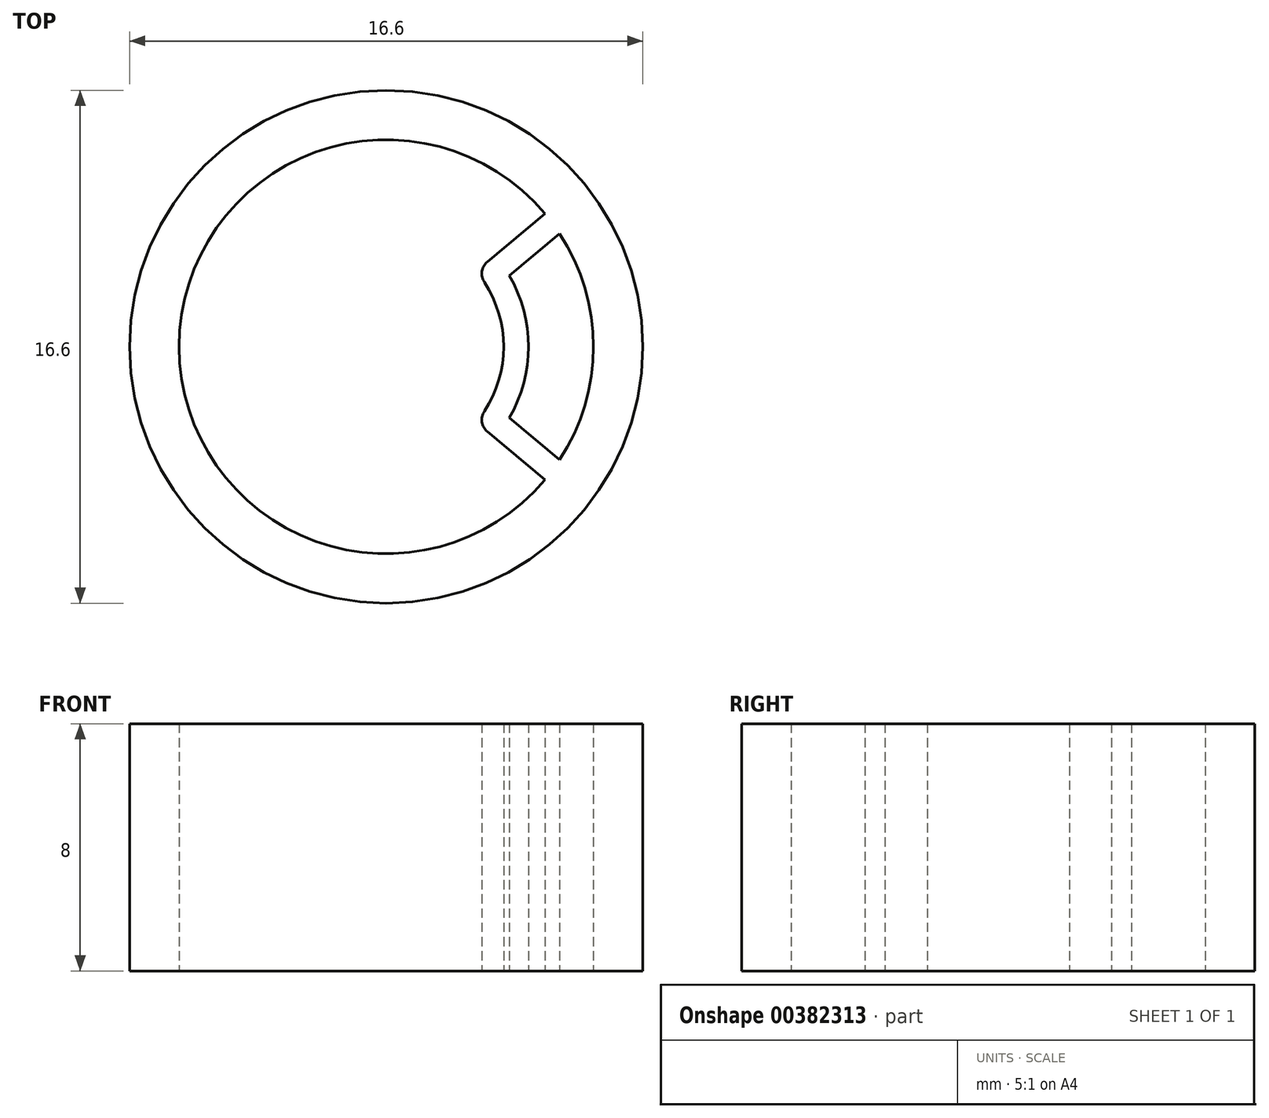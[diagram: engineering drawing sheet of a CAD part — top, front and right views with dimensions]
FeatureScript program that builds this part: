
annotation { "Feature Type Name" : "Feature", "Feature Type Description" : "" }
export const myFeature = defineFeature(function(context is Context, id is Id, definition is map)
    precondition{}
    {
        {
            var Q0;
            Q0=qCreatedBy(makeId("Top.planeOp"),FACE);
            var sketch = newSketch(context, id + "F0", { "sketchPlane" : qUnion([Q0])});
            skCircle(sketch, "E0", {"center": v(0, 0) * mm, "radius": 3.8 * mm});
            skCircle(sketch, "E1", {"center": v(0, 0) * mm, "radius": 6.7 * mm});
            skCircle(sketch, "E2.0", {"center": v(0, 0) * mm, "radius": 8.3 * mm});
            skLineSegment(sketch, "E3", {"start": v(0, 0) * mm, "end": v(6.36, 5.34) * mm});
            skLineSegment(sketch, "E4", {"start": v(0, 0) * mm, "end": v(6.36, -5.34) * mm});
            skCircle(sketch, "E5", {"center": v(0, 0) * mm, "radius": 4.6 * mm});
            skLineSegment(sketch, "E6", {"start": v(3.98, 2.3) * mm, "end": v(5.61, 3.66) * mm});
            skLineSegment(sketch, "E7", {"start": v(3.98, -2.3) * mm, "end": v(5.61, -3.66) * mm});
            skSolve(sketch);
        }
        {
            var Q0;
            {var subQ0=sQuery(id+"F0.wireOp",EDGE,"E3");var subQ1=sQuery(id+"F0.wireOp",EDGE,"E1");var subQ2=makeQuery(id+"F0.imprint","INTERSECT",VERTEX,{"derivedFrom":[subQ1,subQ0]});Q0=makeQuery(id+"F0.imprint","IMPRINT",FACE,{"disambiguationData":[TD([[makeQuery(id+"F0.imprint","IMPRINT",EDGE,{"disambiguationData":[TD([[subQ2,-1.0]])],"derivedFrom":subQ1}),-1.0]])]});}
            var Q1;
            {var subQ0=sQuery(id+"F0.wireOp",EDGE,"E1");var subQ1=makeQuery(id+"F0.imprint","INTERSECT",VERTEX,{"derivedFrom":[subQ0,sQuery(id+"F0.wireOp",EDGE,"E6")]});Q1=makeQuery(id+"F0.imprint","IMPRINT",FACE,{"disambiguationData":[TD([[makeQuery(id+"F0.imprint","IMPRINT",EDGE,{"disambiguationData":[TD([[subQ1,-1.0]])],"derivedFrom":subQ0}),-1.0]])]});}
            var Q2;
            {var subQ0=sQuery(id+"F0.wireOp",EDGE,"E6");Q2=makeQuery(id+"F0.imprint","IMPRINT",FACE,{"disambiguationData":[TD([[makeQuery(id+"F0.imprint","IMPRINT",EDGE,{"derivedFrom":subQ0}),1.0]])]});}
            var Q3;
            {var subQ1=sQuery(id+"F0.wireOp",EDGE,"E0");var subQ5=sQuery(id+"F0.wireOp",EDGE,"E3");var subQ6=makeQuery(id+"F0.imprint","INTERSECT",VERTEX,{"derivedFrom":[subQ1,subQ5]});Q3=makeQuery(id+"F0.imprint","IMPRINT",FACE,{"disambiguationData":[TD([[makeQuery(id+"F0.imprint","IMPRINT",EDGE,{"disambiguationData":[TD([[subQ6,1.0]])],"derivedFrom":subQ1}),-1.0]])]});}
            var Q4;
            {var subQ0=sQuery(id+"F0.wireOp",EDGE,"E7");Q4=makeQuery(id+"F0.imprint","IMPRINT",FACE,{"disambiguationData":[TD([[makeQuery(id+"F0.imprint","IMPRINT",EDGE,{"derivedFrom":subQ0}),-1.0]])]});}
            extrude(context, id + "F1", {"entities" : qUnion([Q0, Q1, Q2, Q3, Q4]), "depth" : 8 * mm});
        }
        {
            var Q0;
            Q0=makeQuery(id+"F1.opExtrude","SWEPT_EDGE",EDGE,{"disambiguationData":[OSD([sQuery(id+"F0.wireOp",EDGE,"E0"),sQuery(id+"F0.wireOp",EDGE,"E3")])]});
            var Q1;
            Q1=makeQuery(id+"F1.opExtrude","SWEPT_EDGE",EDGE,{"disambiguationData":[OSD([sQuery(id+"F0.wireOp",EDGE,"E0"),sQuery(id+"F0.wireOp",EDGE,"E4")])]});
            fillet(context, id + "F2", {"entities" : qUnion([Q0, Q1]), "radius" : .5 * mm, "tangentPropagation" : true, "allowEdgeOverflow" : false});
        }
    });
